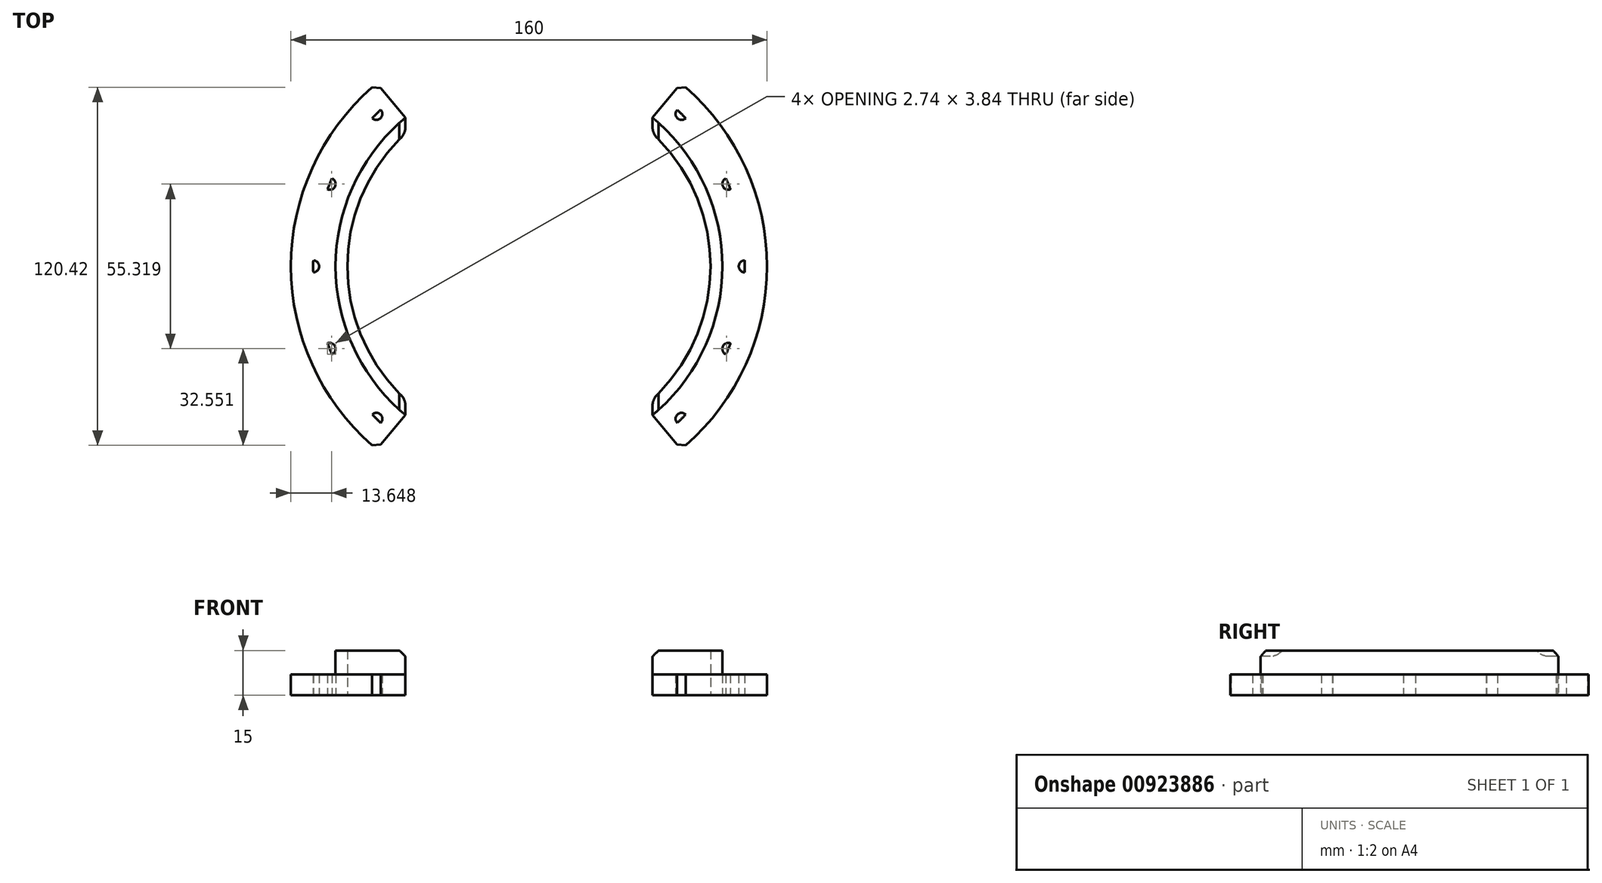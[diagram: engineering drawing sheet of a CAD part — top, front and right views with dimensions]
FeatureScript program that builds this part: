
annotation { "Feature Type Name" : "Feature", "Feature Type Description" : "" }
export const myFeature = defineFeature(function(context is Context, id is Id, definition is map)
    precondition{}
    {
        {
            var Q0;
            Q0=qCreatedBy(makeId("Top.planeOp"),FACE);
            var sketch = newSketch(context, id + "F0", { "sketchPlane" : qUnion([Q0])});
            skArc(sketch, "E0", {"start": v(-55.64, 25) * mm, "mid": v(-61, 0) * mm, "end": v(-55.64, -25) * mm});
            skArc(sketch, "E1.trimOffspring", {"start": v(55.64, -25) * mm, "mid": v(61, 0) * mm, "end": v(55.64, 25) * mm});
            skCircle(sketch, "E2", {"center": v(0, 0) * mm, "radius": 61 * mm});
            skCircle(sketch, "E3", {"center": v(0, 0) * mm, "radius": 65 * mm});
            skLineSegment(sketch, "E4", {"start": v(-41.53, 50) * mm, "end": v(-41.53, -50) * mm});
            skCircle(sketch, "E5", {"center": v(0, 0) * mm, "radius": 80 * mm});
            skLineSegment(sketch, "E6", {"start": v(-41.53, 50) * mm, "end": v(-51.12, 61.54) * mm});
            skLineSegment(sketch, "E7", {"start": v(-41.53, -50) * mm, "end": v(-51.12, -61.54) * mm});
            skArc(sketch, "E8", {"start": v(-46.33, -55.77) * mm, "mid": v(-72.5, 0) * mm, "end": v(-46.33, 55.77) * mm});
            skCircle(sketch, "E9", {"center": v(-72.5, 0) * mm, "radius": 2 * mm});
            skCircle(sketch, "E10.1.0", {"center": v(-66.98, -27.74) * mm, "radius": 2 * mm});
            skCircle(sketch, "E10.2.0", {"center": v(-51.27, -51.27) * mm, "radius": 2 * mm});
            skCircle(sketch, "E11.1.3.0", {"center": v(-27.74, -66.98) * mm, "radius": 2 * mm});
            skCircle(sketch, "E11.1.4.0", {"center": v(0, -72.5) * mm, "radius": 2 * mm});
            skCircle(sketch, "E11.1.5.0", {"center": v(27.74, -66.98) * mm, "radius": 2 * mm});
            skCircle(sketch, "E11.1.6.0", {"center": v(51.27, -51.27) * mm, "radius": 2 * mm});
            skCircle(sketch, "E11.1.7.0", {"center": v(66.98, -27.74) * mm, "radius": 2 * mm});
            skCircle(sketch, "E12.1.8.0", {"center": v(72.5, 0) * mm, "radius": 2 * mm});
            skCircle(sketch, "E12.1.9.0", {"center": v(66.98, 27.74) * mm, "radius": 2 * mm});
            skCircle(sketch, "E12.1.10.0", {"center": v(51.27, 51.27) * mm, "radius": 2 * mm});
            skCircle(sketch, "E12.1.11.0", {"center": v(27.74, 66.98) * mm, "radius": 2 * mm});
            skCircle(sketch, "E13.1.12.0", {"center": v(0, 72.5) * mm, "radius": 2 * mm});
            skCircle(sketch, "E13.1.13.0", {"center": v(-27.74, 66.98) * mm, "radius": 2 * mm});
            skCircle(sketch, "E13.1.14.0", {"center": v(-51.27, 51.27) * mm, "radius": 2 * mm});
            skCircle(sketch, "E13.1.15.0", {"center": v(-66.98, 27.74) * mm, "radius": 2 * mm});
            skSolve(sketch);
        }
        {
            var Q0;
            {var subQ0=sQuery(id+"F0.wireOp",EDGE,"E2");var subQ4=makeQuery(id+"F0.imprint","IMPRINT",VERTEX,{"disambiguationData":[OD(1.0)],"derivedFrom":subQ0});Q0=makeQuery(id+"F0.imprint","IMPRINT",FACE,{"disambiguationData":[TD([[makeQuery(id+"F0.imprint","IMPRINT",EDGE,{"disambiguationData":[TD([[subQ4,-1.0]])],"derivedFrom":subQ0}),-1.0]])]});}
            extrude(context, id + "F1", {"entities" : qUnion([Q0]), "depth" : 15 * mm, "offsetDistance" : 25 * mm});
        }
        {
            var Q0;
            {var subQ1=sQuery(id+"F0.wireOp",EDGE,"E8");var subQ8=sQuery(id+"F0.wireOp",EDGE,"E7");var subQ22=makeQuery(id+"F0.imprint","INTERSECT",VERTEX,{"derivedFrom":[subQ8,subQ1]});Q0=makeQuery(id+"F0.imprint","IMPRINT",FACE,{"disambiguationData":[TD([[makeQuery(id+"F0.imprint","IMPRINT",EDGE,{"disambiguationData":[TD([[subQ22,-1.0]])],"derivedFrom":subQ1}),-1.0]])]});}
            var Q1;
            {var subQ11=sQuery(id+"F0.wireOp",EDGE,"E6");var subQ12=sQuery(id+"F0.wireOp",EDGE,"E5");var subQ13=makeQuery(id+"F0.imprint","INTERSECT",VERTEX,{"derivedFrom":[subQ12,subQ11]});Q1=makeQuery(id+"F0.imprint","IMPRINT",FACE,{"disambiguationData":[TD([[makeQuery(id+"F0.imprint","IMPRINT",EDGE,{"disambiguationData":[TD([[subQ13,-1.0]])],"derivedFrom":subQ12}),1.0]])]});}
            extrude(context, id + "F2", {"entities" : qUnion([Q0, Q1]), "operationType" : NewBodyOperationType.ADD, "depth" : 7 * mm, "offsetDistance" : 25 * mm});
        }
        {
            var Q0;
            {var subQ0=sQuery(id+"F0.wireOp",EDGE,"E4");Q0=makeQuery(id+"F1.opExtrude","CAP_EDGE",EDGE,{"disambiguationData":[OSD([subQ0]),TDD([makeQuery(id+"F0.imprint","IMPRINT",EDGE,{"disambiguationData":[TD([[makeQuery(id+"F0.imprint","INTERSECT",VERTEX,{"disambiguationData":[OD(1.0)],"derivedFrom":[sQuery(id+"F0.wireOp",EDGE,"E2"),subQ0]}),-1.0]])],"derivedFrom":subQ0})])],"isStart":false});}
            var Q1;
            {var subQ0=sQuery(id+"F0.wireOp",EDGE,"E4");Q1=makeQuery(id+"F1.opExtrude","CAP_EDGE",EDGE,{"disambiguationData":[OSD([subQ0]),TDD([makeQuery(id+"F0.imprint","IMPRINT",EDGE,{"disambiguationData":[TD([[makeQuery(id+"F0.imprint","INTERSECT",VERTEX,{"disambiguationData":[OD(0.0)],"derivedFrom":[sQuery(id+"F0.wireOp",EDGE,"E2"),subQ0]}),1.0]])],"derivedFrom":subQ0})])],"isStart":false});}
            var Q2;
            Q2=makeQuery(id+"F2.opExtrude","SWEPT_EDGE",EDGE,{"disambiguationData":[OSD([sQuery(id+"F0.wireOp",EDGE,"E5"),sQuery(id+"F0.wireOp",EDGE,"E6")])]});
            var Q3;
            Q3=makeQuery(id+"F2.opExtrude","SWEPT_EDGE",EDGE,{"disambiguationData":[OSD([sQuery(id+"F0.wireOp",EDGE,"E5"),sQuery(id+"F0.wireOp",EDGE,"E7")])]});
            chamfer(context, id + "F3", {"entities" : qUnion([Q0, Q1, Q2, Q3]), "width" : 2 * mm, "tangentPropagation" : true});
        }
        {
            var Q0;
            {var subQ0=sQuery(id+"F0.wireOp",EDGE,"E4");var subQ1=sQuery(id+"F0.wireOp",EDGE,"E2");Q0=makeQuery(id+"F1.opExtrude","SWEPT_EDGE",EDGE,{"disambiguationData":[OSD([subQ1,subQ0]),TDD([makeQuery(id+"F0.imprint","INTERSECT",VERTEX,{"disambiguationData":[OD(0.0)],"derivedFrom":[subQ1,subQ0]})])]});}
            var Q1;
            {var subQ0=sQuery(id+"F0.wireOp",EDGE,"E4");var subQ1=sQuery(id+"F0.wireOp",EDGE,"E2");Q1=makeQuery(id+"F1.opExtrude","SWEPT_EDGE",EDGE,{"disambiguationData":[OSD([subQ1,subQ0]),TDD([makeQuery(id+"F0.imprint","INTERSECT",VERTEX,{"disambiguationData":[OD(1.0)],"derivedFrom":[subQ1,subQ0]})])]});}
            fillet(context, id + "F4", {"entities" : qUnion([Q0, Q1]), "radius" : 5 * mm, "tangentPropagation" : true, "allowEdgeOverflow" : false});
        }
        {
            var Q0;
            Q0=makeQuery(id+"F1.opExtrude","SWEPT_BODY",BODY,{"disambiguationData":[OSD([sQuery(id+"F0.wireOp",EDGE,"E2"),sQuery(id+"F0.wireOp",EDGE,"E3"),sQuery(id+"F0.wireOp",EDGE,"E4")])]});
            var Q1;
            Q1=qCreatedBy(makeId("Right.planeOp"),FACE);
            mirror(context, id + "F5", {"entities" : qUnion([Q0]), "mirrorPlane" : qUnion([Q1])});
        }
    });
